# Revit family: Distanzhülse - DHI 080
name_source: partatom
category: Generic Models
revit_build: Autodesk Revit 2017 (Build: 20190508_0315(x64)
units: mm (PartAtom-declared; Revit-internal decimal feet)

## family parameters
Always vertical = Yes
Can host rebar = No
Cut with Voids When Loaded = No
Part Type = Normal
Room Calculation Point = No
Round Connector Dimension = Use Diameter
Shared = No
Work Plane-Based = No

## types (11) — shared parameters
Manufacturer = OBO BETTERMANN
Material = Hot-dip galvanised
URL = http://www.obo-bettermann.com

## per-type parameters (varying)
| type | Article Type | GTIN | Length | Manufacturer Art.No. |
| DHI 050 | DHI 060 | 4012196397228 | 50 mm  [stored 0.164042 ft] | 7205901 |
| DHI 060 | DHI 060 | 4012196397235 | 60 mm  [stored 0.19685 ft] | 7205901 |
| DHI 070 | DHI 070 | 4012196397242 | 70 mm  [stored 0.229659 ft] | 7205902 |
| DHI 080 | DHI 080 | 4012196397266 | 80 mm  [stored 0.262467 ft] | 7205903 |
| DHI 090 | DHI 090 | 4012196397297 | 90 mm  [stored 0.295276 ft] | 7205904 |
| DHI 100 | DHI 100 | 4012196397303 | 100 mm  [stored 0.328084 ft] | 7205905 |
| DHI 110 | DHI 110 | 4012196397310 | 110 mm  [stored 0.360892 ft] | 7205906 |
| DHI 120 | DHI 120 | 4012196397327 | 120 mm  [stored 0.393701 ft] | 7205907 |
| DHI 130 | DHI 130 | 4012196397358 | 130 mm  [stored 0.426509 ft] | 7205908 |
| DHI 140 | DHI 140 | 4012196397365 | 140 mm  [stored 0.459318 ft] | 7205909 |
| DHI 150 | DHI 150 | 4012196397372 | 150 mm | 7205910 |

note: [stored X ft] marks values corroborated as IEEE doubles in the binary element streams (Revit-internal decimal feet)

## geometry (parser evidence)
native form markers: Sweep x3
no freeform markers — native parametric forms only
